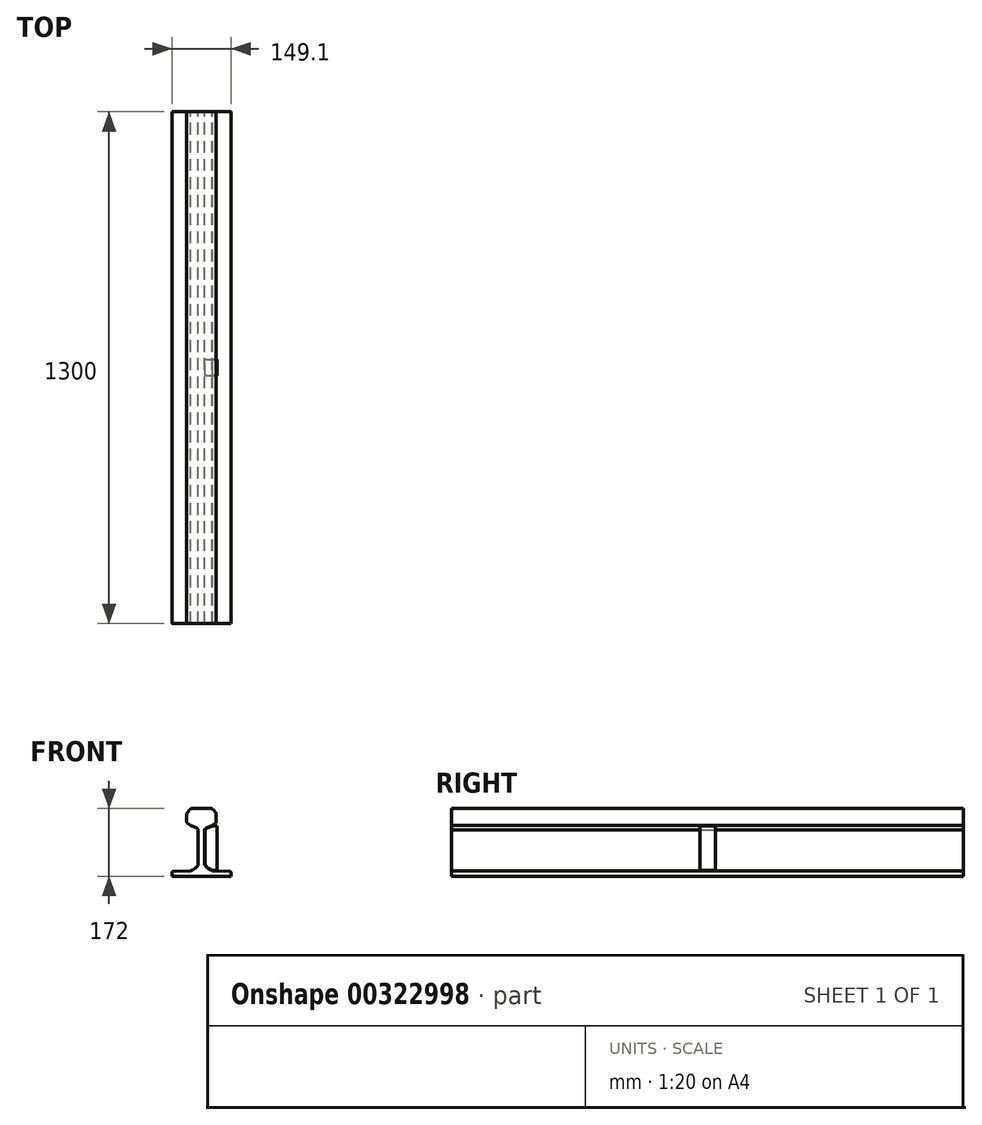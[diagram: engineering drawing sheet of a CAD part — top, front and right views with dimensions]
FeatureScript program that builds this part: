
annotation { "Feature Type Name" : "Feature", "Feature Type Description" : "" }
export const myFeature = defineFeature(function(context is Context, id is Id, definition is map)
    precondition{}
    {
        {
            var Q0;
            Q0=qCreatedBy(makeId("Front.planeOp"),FACE);
            var sketch = newSketch(context, id + "F0", { "sketchPlane" : qUnion([Q0])});
            skLineSegment(sketch, "E0", {"start": v(-10.77, 99.61) * mm, "end": v(-10.77, -103.46) * mm, "construction": true});
            skPoint(sketch, "E1", {"position": v(-86.22, -75.65) * mm});
            skLineSegment(sketch, "E2", {"start": v(-86.22, -75.65) * mm, "end": v(63.78, -75.65) * mm});
            skLineSegment(sketch, "E3", {"start": v(63.78, -75.65) * mm, "end": v(63.78, -66.07) * mm});
            skLineSegment(sketch, "E4", {"start": v(61.86, -64.07) * mm, "end": v(16.54, -62.24) * mm});
            skLineSegment(sketch, "E5", {"start": v(16.54, -62.24) * mm, "end": v(11.83, -59.9) * mm});
            skLineSegment(sketch, "E6", {"start": v(2.23, 47.15) * mm, "end": v(17.09, 53.37) * mm});
            skLineSegment(sketch, "E7", {"start": v(10.83, 96.35) * mm, "end": v(-10.77, 96.35) * mm});
            skLineSegment(sketch, "E8", {"start": v(26.68, 79.78) * mm, "end": v(26.68, 62.41) * mm});
            skLineSegment(sketch, "E9", {"start": v(25.54, 60.06) * mm, "end": v(17.09, 53.37) * mm});
            skLineSegment(sketch, "E10", {"start": v(23.84, 87.88) * mm, "end": v(21, 91.46) * mm});
            skLineSegment(sketch, "E11", {"start": v(-10.77, 3.53) * mm, "end": v(-2.52, 3.53) * mm});
            skLineSegment(sketch, "E12", {"start": v(-2.52, 41.69) * mm, "end": v(-2.52, -46.1) * mm});
            skLineSegment(sketch, "E13", {"start": v(-2.52, 41.69) * mm, "end": v(-1.18, 44.1) * mm});
            skLineSegment(sketch, "E14.MirrorCS", {"start": v(-32.37, 96.35) * mm, "end": v(-10.77, 96.35) * mm});
            skLineSegment(sketch, "E15.MirrorCS", {"start": v(-45.39, 87.88) * mm, "end": v(-42.54, 91.46) * mm});
            skLineSegment(sketch, "E16.MirrorCS", {"start": v(-47.09, 60.06) * mm, "end": v(-38.63, 53.37) * mm});
            skLineSegment(sketch, "E17.MirrorCS", {"start": v(-23.78, 47.15) * mm, "end": v(-38.63, 53.37) * mm});
            skLineSegment(sketch, "E18.MirrorCS", {"start": v(-48.22, 79.78) * mm, "end": v(-48.22, 62.41) * mm});
            skLineSegment(sketch, "E19.MirrorCS", {"start": v(-19.02, 41.69) * mm, "end": v(-20.37, 44.1) * mm});
            skLineSegment(sketch, "E20.MirrorCS", {"start": v(-19.02, 41.69) * mm, "end": v(-19.02, -46.1) * mm});
            skLineSegment(sketch, "E21.MirrorCS", {"start": v(-38.08, -62.24) * mm, "end": v(-33.38, -59.9) * mm});
            skLineSegment(sketch, "E22.MirrorCS", {"start": v(-83.4, -64.07) * mm, "end": v(-38.08, -62.24) * mm});
            skLineSegment(sketch, "E23.MirrorCS", {"start": v(-85.32, -75.65) * mm, "end": v(-85.32, -66.07) * mm});
            skPoint(sketch, "E24.visualSharp", {"position": v(-38.63, 96.35) * mm});
            skArc(sketch, "E24.filletArc", {"start": v(-32.37, 96.35) * mm, "mid": v(-38.01, 95.06) * mm, "end": v(-42.54, 91.46) * mm});
            skPoint(sketch, "E25.visualSharp", {"position": v(17.09, 96.35) * mm});
            skArc(sketch, "E25.filletArc", {"start": v(21, 91.46) * mm, "mid": v(16.47, 95.06) * mm, "end": v(10.83, 96.35) * mm});
            skPoint(sketch, "E26.visualSharp", {"position": v(-48.22, 84.32) * mm});
            skArc(sketch, "E26.filletArc", {"start": v(-45.39, 87.88) * mm, "mid": v(-47.5, 84.07) * mm, "end": v(-48.22, 79.78) * mm});
            skPoint(sketch, "E27.visualSharp", {"position": v(26.68, 84.32) * mm});
            skArc(sketch, "E27.filletArc", {"start": v(26.68, 79.78) * mm, "mid": v(25.95, 84.07) * mm, "end": v(23.84, 87.88) * mm});
            skPoint(sketch, "E28.visualSharp", {"position": v(-48.22, 60.96) * mm});
            skArc(sketch, "E28.filletArc", {"start": v(-48.22, 62.41) * mm, "mid": v(-47.92, 61.1) * mm, "end": v(-47.09, 60.06) * mm});
            skPoint(sketch, "E29.visualSharp", {"position": v(26.68, 60.96) * mm});
            skArc(sketch, "E29.filletArc", {"start": v(25.54, 60.06) * mm, "mid": v(26.38, 61.1) * mm, "end": v(26.68, 62.41) * mm});
            skPoint(sketch, "E30.visualSharp", {"position": v(0, 46.21) * mm});
            skArc(sketch, "E30.filletArc", {"start": v(2.23, 47.15) * mm, "mid": v(0.27, 45.9) * mm, "end": v(-1.18, 44.1) * mm});
            skPoint(sketch, "E31.visualSharp", {"position": v(-21.55, 46.21) * mm});
            skArc(sketch, "E31.filletArc", {"start": v(-20.37, 44.1) * mm, "mid": v(-21.82, 45.9) * mm, "end": v(-23.78, 47.15) * mm});
            skPoint(sketch, "E32.visualSharp", {"position": v(-85.32, -64.15) * mm});
            skArc(sketch, "E32.filletArc", {"start": v(-83.4, -64.07) * mm, "mid": v(-84.77, -64.69) * mm, "end": v(-85.32, -66.07) * mm});
            skPoint(sketch, "E33.visualSharp", {"position": v(63.78, -64.15) * mm});
            skArc(sketch, "E33.filletArc", {"start": v(63.78, -66.07) * mm, "mid": v(63.22, -64.69) * mm, "end": v(61.86, -64.07) * mm});
            skArc(sketch, "E34.filletArc", {"start": v(-33.38, -59.9) * mm, "mid": v(-25.48, -54.5) * mm, "end": v(-19.33, -47.17) * mm});
            skArc(sketch, "E35.filletArc", {"start": v(-19.33, -47.17) * mm, "mid": v(-19.1, -46.66) * mm, "end": v(-19.02, -46.1) * mm});
            skPoint(sketch, "E36.visualSharp", {"position": v(0, -54) * mm});
            skArc(sketch, "E36.filletArc", {"start": v(-2.22, -47.17) * mm, "mid": v(3.93, -54.5) * mm, "end": v(11.83, -59.9) * mm});
            skPoint(sketch, "E37.visualSharp", {"position": v(-2.52, -46.67) * mm});
            skArc(sketch, "E37.filletArc", {"start": v(-2.52, -46.1) * mm, "mid": v(-2.45, -46.66) * mm, "end": v(-2.22, -47.17) * mm});
            skLineSegment(sketch, "E38.0", {"start": v(2.66, 46.13) * mm, "end": v(17.51, 52.36) * mm});
            skArc(sketch, "E38.1", {"start": v(2.66, 46.13) * mm, "mid": v(1, 45.09) * mm, "end": v(-0.22, 43.56) * mm});
            skLineSegment(sketch, "E38.2", {"start": v(-1.42, 41.4) * mm, "end": v(-0.22, 43.56) * mm});
            skLineSegment(sketch, "E38.3", {"start": v(-1.42, 41.4) * mm, "end": v(-1.42, -46.1) * mm});
            skLineSegment(sketch, "E38.5", {"start": v(16.82, -61.15) * mm, "end": v(12.32, -58.9) * mm});
            skArc(sketch, "E38.6", {"start": v(-1.29, -46.58) * mm, "mid": v(4.67, -53.69) * mm, "end": v(12.32, -58.9) * mm});
            skArc(sketch, "E38.7", {"start": v(-1.42, -46.1) * mm, "mid": v(-1.39, -46.35) * mm, "end": v(-1.29, -46.58) * mm});
            skLineSegment(sketch, "E39.0", {"start": v(28.24, -61.61) * mm, "end": v(16.82, -61.15) * mm});
            skLineSegment(sketch, "E40", {"start": v(17.51, 52.36) * mm, "end": v(28.24, 52.36) * mm});
            skLineSegment(sketch, "E41", {"start": v(28.24, 52.36) * mm, "end": v(28.24, -61.61) * mm});
            skSolve(sketch);
        }
        {
            var Q0;
            Q0=qSketchRegion(id+"F0",true);
            extrude(context, id + "F1", {"entities" : qUnion([Q0]), "depth" : 1300 * mm, "symmetric" : true});
        }
        {
            var Q0;
            Q0=makeQuery(id+"F0.imprint","IMPRINT",FACE,{"disambiguationData":[TD([[makeQuery(id+"F0.imprint","IMPRINT",EDGE,{"derivedFrom":sQuery(id+"F0.wireOp",EDGE,"E38.0")}),-1.0]])]});
            extrude(context, id + "F2", {"entities" : qUnion([Q0]), "operationType" : NewBodyOperationType.REMOVE, "oppositeDirection" : true, "depth" : 1300 * mm, "symmetric" : true});
        }
        {
            var Q0;
            Q0=makeQuery(id+"F0.imprint","IMPRINT",FACE,{"disambiguationData":[TD([[makeQuery(id+"F0.imprint","IMPRINT",EDGE,{"derivedFrom":sQuery(id+"F0.wireOp",EDGE,"E38.0")}),-1.0]])]});
            extrude(context, id + "F3", {"entities" : qUnion([Q0]), "depth" : 40 * mm, "symmetric" : true});
        }
    });
